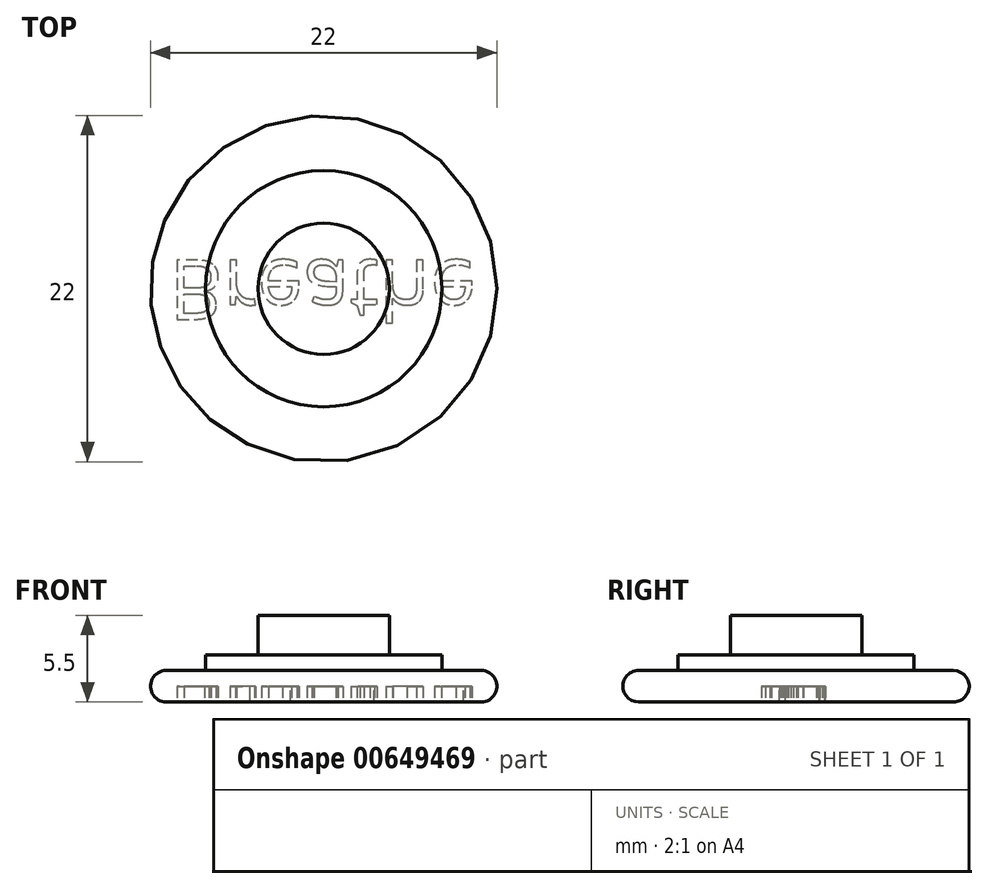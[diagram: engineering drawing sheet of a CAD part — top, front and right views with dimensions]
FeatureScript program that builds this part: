
annotation { "Feature Type Name" : "Feature", "Feature Type Description" : "" }
export const myFeature = defineFeature(function(context is Context, id is Id, definition is map)
    precondition{}
    {
        {
            var Q0;
            Q0=qCreatedBy(makeId("Top.planeOp"),FACE);
            var sketch = newSketch(context, id + "F0", { "sketchPlane" : qUnion([Q0])});
            skCircle(sketch, "E0", {"center": v(0, 0) * mm, "radius": 11 * mm});
            skCircle(sketch, "E1", {"center": v(0, 0) * mm, "radius": 7.5 * mm});
            skCircle(sketch, "E2", {"center": v(0, 0) * mm, "radius": 4.17 * mm});
            skSolve(sketch);
        }
        {
            var Q0;
            Q0=makeQuery(id+"F0.imprint","IMPRINT",FACE,{"disambiguationData":[TD([[makeQuery(id+"F0.imprint","IMPRINT",EDGE,{"derivedFrom":sQuery(id+"F0.wireOp",EDGE,"E0")}),1.0]])]});
            extrude(context, id + "F1", {"entities" : qUnion([Q0]), "depth" : 2 * mm, "offsetDistance" : 25 * mm});
        }
        {
            var Q0;
            Q0=makeQuery(id+"F0.imprint","IMPRINT",FACE,{"disambiguationData":[TD([[makeQuery(id+"F0.imprint","IMPRINT",EDGE,{"derivedFrom":sQuery(id+"F0.wireOp",EDGE,"E1")}),1.0]])]});
            extrude(context, id + "F2", {"entities" : qUnion([Q0]), "operationType" : NewBodyOperationType.ADD, "depth" : 3 * mm, "offsetDistance" : 25 * mm});
        }
        {
            var Q0;
            Q0=makeQuery(id+"F0.imprint","IMPRINT",FACE,{"disambiguationData":[TD([[makeQuery(id+"F0.imprint","IMPRINT",EDGE,{"derivedFrom":sQuery(id+"F0.wireOp",EDGE,"E2")}),1.0]])]});
            extrude(context, id + "F3", {"entities" : qUnion([Q0]), "operationType" : NewBodyOperationType.ADD, "depth" : 5.5 * mm, "offsetDistance" : 25 * mm});
        }
        {
            var Q0;
            Q0=makeQuery(id+"F1.opExtrude","CAP_EDGE",EDGE,{"disambiguationData":[OSD([sQuery(id+"F0.wireOp",EDGE,"E0")])],"isStart":false});
            var Q1;
            Q1=makeQuery(id+"F1.opExtrude","CAP_EDGE",EDGE,{"disambiguationData":[OSD([sQuery(id+"F0.wireOp",EDGE,"E0")])],"isStart":true});
            fillet(context, id + "F4", {"entities" : qUnion([Q0, Q1]), "radius" : 1 * mm, "tangentPropagation" : true, "allowEdgeOverflow" : false});
        }
        {
            var Q0;
            {var subQ0=sQuery(id+"F0.wireOp",EDGE,"E2");var subQ1=sQuery(id+"F0.wireOp",EDGE,"E1");Q0=makeQuery(id+"F3.boolean.opBoolean","MERGE",FACE,{"derivedFrom":[makeQuery(id+"F2.boolean.opBoolean","MERGE",FACE,{"derivedFrom":[makeQuery(id+"F1.opExtrude","CAP_FACE",FACE,{"disambiguationData":[OSD([sQuery(id+"F0.wireOp",EDGE,"E0"),subQ1])],"isStart":true}),makeQuery(id+"F2.opExtrude","CAP_FACE",FACE,{"disambiguationData":[OSD([subQ1,subQ0])],"isStart":true})]}),makeQuery(id+"F3.opExtrude","CAP_FACE",FACE,{"disambiguationData":[OSD([subQ0])],"isStart":true})]});}
            var sketch = newSketch(context, id + "F5", { "sketchPlane" : qUnion([Q0])});
            skText(sketch, "E3", { "text": "Breathe", "fontName": "OpenSans-Regular.ttf"});
            const initialGuessF5  = {"E3": [-0.00983, -0.00182, 1, 0, 0.0038]};
            skSetInitialGuess(sketch, initialGuessF5);
            skSolve(sketch);
        }
        {
            var Q0;
            Q0 = qSketchRegion(id + "F5", true);
            extrude(context, id + "F6", {"entities" : qUnion([Q0]), "operationType" : NewBodyOperationType.REMOVE, "oppositeDirection" : true, "depth" : 1 * mm, "offsetDistance" : 25 * mm});
        }
    });
